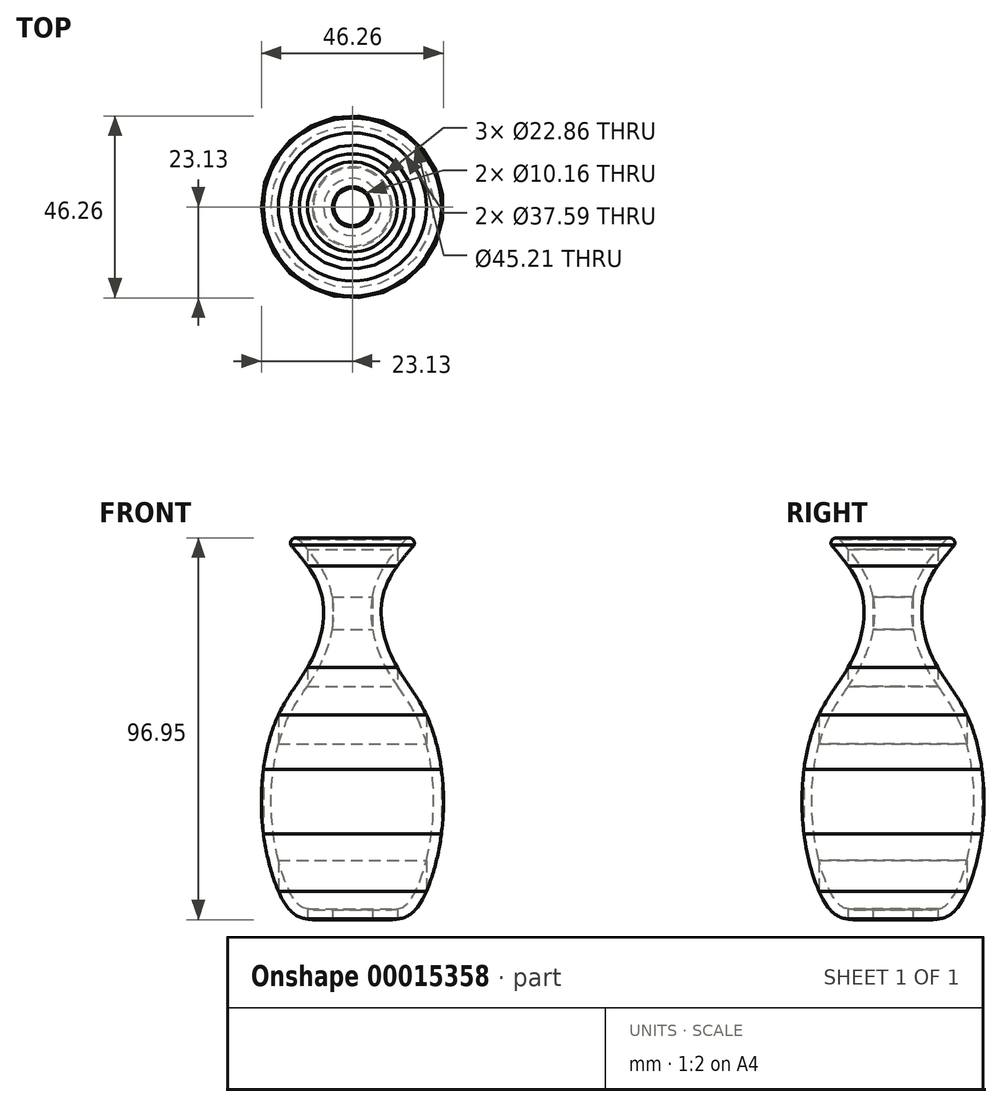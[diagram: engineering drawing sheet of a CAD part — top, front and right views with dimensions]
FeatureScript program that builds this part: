
annotation { "Feature Type Name" : "Feature", "Feature Type Description" : "" }
export const myFeature = defineFeature(function(context is Context, id is Id, definition is map)
    precondition{}
    {
        {
            var Q0;
            Q0=qCreatedBy(makeId("Top.planeOp"),FACE);
            var sketch = newSketch(context, id + "F0", { "sketchPlane" : qUnion([Q0])});
            skCircle(sketch, "E0", {"center": v(0, 0) * mm, "radius": 28.58 * mm});
            skCircle(sketch, "E1", {"center": v(0, 0) * mm, "radius": 12.7 * mm});
            skCircle(sketch, "E2", {"center": v(0, 0) * mm, "radius": 47 * mm});
            skCircle(sketch, "E3", {"center": v(0, 0) * mm, "radius": 56.52 * mm});
            skCircle(sketch, "E4", {"center": v(0, 0) * mm, "radius": 63.5 * mm});
            skSolve(sketch);
        }
        {
            var Q0;
            Q0 = qSketchRegion(id + "F0", true);
            extrude(context, id + "F1", {"entities" : qUnion([Q0]), "depth" : 254 * mm});
        }
        {
            var Q0;
            Q0=makeQuery(id+"F0.imprint","IMPRINT",FACE,{"disambiguationData":[TD([[makeQuery(id+"F0.imprint","IMPRINT",EDGE,{"derivedFrom":sQuery(id+"F0.wireOp",EDGE,"E2")}),-1.0]])]});
            var Q1;
            Q1=makeQuery(id+"F0.imprint","IMPRINT",FACE,{"disambiguationData":[TD([[makeQuery(id+"F0.imprint","IMPRINT",EDGE,{"derivedFrom":sQuery(id+"F0.wireOp",EDGE,"E0")}),1.0]])]});
            extrude(context, id + "F2", {"entities" : qUnion([Q0, Q1]), "depth" : 254 * mm});
        }
        {
            var Q0;
            Q0=makeQuery(id+"F0.imprint","IMPRINT",FACE,{"disambiguationData":[TD([[makeQuery(id+"F0.imprint","IMPRINT",EDGE,{"derivedFrom":sQuery(id+"F0.wireOp",EDGE,"E0")}),-1.0]])]});
            var Q1;
            Q1=makeQuery(id+"F0.imprint","IMPRINT",FACE,{"disambiguationData":[TD([[makeQuery(id+"F0.imprint","IMPRINT",EDGE,{"derivedFrom":sQuery(id+"F0.wireOp",EDGE,"E1")}),1.0]])]});
            extrude(context, id + "F3", {"entities" : qUnion([Q0, Q1]), "depth" : 254 * mm});
        }
        {
            var Q0;
            Q0=qCreatedBy(makeId("Front.planeOp"),FACE);
            var sketch = newSketch(context, id + "F4", { "sketchPlane" : qUnion([Q0])});
            skLineSegment(sketch, "E5", {"start": v(25.4, 0) * mm, "end": v(-23.74, 0) * mm});
            skFitSpline(sketch, "E6", {"points": [v(25.4, 0) * mm, v(38.83, 5.12) * mm, v(57.14, 60.04) * mm, v(47.11, 129.79) * mm, v(25.4, 165.97) * mm, v(19.65, 206.94) * mm, v(41.88, 241.3) * mm], "startDerivative": vector(142.07, 14.8) * mm, "endDerivative": vector(170.63, 209.79) * mm});
            skLineSegment(sketch, "E7", {"start": v(0, 241.3) * mm, "end": v(0, 0) * mm});
            skFitSpline(sketch, "E8.0", {"points": [v(24.74, 6.32) * mm, v(25.48, 6.4) * mm, v(26.87, 6.55) * mm, v(28.68, 6.82) * mm, v(30.23, 7.18) * mm, v(31.57, 7.67) * mm, v(32.6, 8.24) * mm, v(33.46, 8.84) * mm, v(34, 9.3) * mm, v(34.46, 9.74) * mm, v(34.93, 10.22) * mm, v(35.56, 10.93) * mm, v(36.36, 11.95) * mm, v(37.45, 13.51) * mm, v(38.85, 15.83) * mm, v(40.53, 19.14) * mm, v(42.16, 22.9) * mm, v(44.25, 28.42) * mm, v(46.61, 36.18) * mm, v(48.91, 46.4) * mm, v(50.29, 55.33) * mm, v(51, 62.52) * mm, v(51.46, 69.72) * mm, v(51.55, 78.66) * mm, v(50.93, 89.17) * mm, v(49.63, 99.3) * mm, v(47.68, 108.9) * mm, v(45.56, 116.33) * mm, v(43.6, 121.84) * mm, v(42, 125.74) * mm, v(40.3, 129.37) * mm, v(38.45, 132.84) * mm, v(36.5, 136.18) * mm, v(33.77, 140.5) * mm, v(30.19, 145.8) * mm, v(26.53, 151.22) * mm, v(23.68, 155.79) * mm, v(21.96, 158.77) * mm, v(20.64, 161.25) * mm, v(19.69, 163.16) * mm, v(18.77, 165.12) * mm, v(17.62, 167.78) * mm, v(16.3, 171.2) * mm, v(14.47, 176.84) * mm, v(12.75, 184.1) * mm, v(11.93, 191.53) * mm, v(11.9, 197.46) * mm, v(12.21, 201.88) * mm, v(12.78, 205.52) * mm, v(13.44, 208.4) * mm, v(14.23, 211.22) * mm, v(15.45, 214.6) * mm, v(17.82, 219.78) * mm, v(21.42, 225.79) * mm, v(26.38, 232.5) * mm, v(31.66, 238.93) * mm, v(35.2, 243.17) * mm, v(36.95, 245.31) * mm]});
            skLineSegment(sketch, "E9", {"start": v(24.74, 6.32) * mm, "end": v(0, 6.32) * mm});
            skLineSegment(sketch, "E10", {"start": v(0, 241.3) * mm, "end": v(33.56, 241.2) * mm});
            skArc(sketch, "E11", {"start": v(33.56, 241.2) * mm, "mid": v(37.7, 241.95) * mm, "end": v(39.15, 237.98) * mm});
            skSolve(sketch);
        }
        {
            var Q0;
            {var subQ8=sQuery(id+"F4.wireOp",EDGE,"E6");Q0=makeQuery(id+"F4.imprint","IMPRINT",FACE,{"disambiguationData":[TD([[makeQuery(id+"F4.imprint","IMPRINT",EDGE,{"derivedFrom":subQ8}),1.0]])]});}
            var Q1;
            Q1=sQuery(id+"F4.wireOp",EDGE,"E7");
            revolve(context, id + "F5", {"operationType" : NewBodyOperationType.INTERSECT, "entities" : qUnion([Q0]), "axis" : qUnion([Q1]), "revolveType" : RevolveType.FULL, "oppositeDirection" : true});
        }
        {
            var Q0;
            Q0=makeQuery(id+"F1.opExtrude","SWEPT_BODY",BODY,{"disambiguationData":[OSD([sQuery(id+"F0.wireOp",EDGE,"E3"),sQuery(id+"F0.wireOp",EDGE,"E4")])]});
            var Q1;
            Q1=makeQuery(id+"F2.opExtrude","SWEPT_BODY",BODY,{"disambiguationData":[OSD([sQuery(id+"F0.wireOp",EDGE,"E2"),sQuery(id+"F0.wireOp",EDGE,"E3")])]});
            var Q2;
            Q2=makeQuery(id+"F5.boolean.opBoolean","SPLIT",BODY,{"disambiguationData":[OD(0.0)],"derivedFrom":makeQuery(id+"F2.opExtrude","SWEPT_BODY",BODY,{"disambiguationData":[OSD([sQuery(id+"F0.wireOp",EDGE,"E0"),sQuery(id+"F0.wireOp",EDGE,"E1")])]})});
            var Q3;
            Q3=makeQuery(id+"F5.boolean.opBoolean","SPLIT",BODY,{"disambiguationData":[OD(1.0)],"derivedFrom":makeQuery(id+"F2.opExtrude","SWEPT_BODY",BODY,{"disambiguationData":[OSD([sQuery(id+"F0.wireOp",EDGE,"E0"),sQuery(id+"F0.wireOp",EDGE,"E1")])]})});
            var Q4;
            Q4=makeQuery(id+"F5.boolean.opBoolean","SPLIT",BODY,{"disambiguationData":[OD(0.0)],"derivedFrom":makeQuery(id+"F3.opExtrude","SWEPT_BODY",BODY,{"disambiguationData":[OSD([sQuery(id+"F0.wireOp",EDGE,"E0"),sQuery(id+"F0.wireOp",EDGE,"E2")])]})});
            var Q5;
            Q5=makeQuery(id+"F5.boolean.opBoolean","SPLIT",BODY,{"disambiguationData":[OD(0.0)],"derivedFrom":makeQuery(id+"F3.opExtrude","SWEPT_BODY",BODY,{"disambiguationData":[OSD([sQuery(id+"F0.wireOp",EDGE,"E1")])]})});
            var Q6;
            Q6=makeQuery(id+"F5.boolean.opBoolean","SPLIT",BODY,{"disambiguationData":[OD(1.0)],"derivedFrom":makeQuery(id+"F3.opExtrude","SWEPT_BODY",BODY,{"disambiguationData":[OSD([sQuery(id+"F0.wireOp",EDGE,"E1")])]})});
            var Q7;
            Q7=makeQuery(id+"F5.boolean.opBoolean","SPLIT",BODY,{"disambiguationData":[OD(1.0)],"derivedFrom":makeQuery(id+"F3.opExtrude","SWEPT_BODY",BODY,{"disambiguationData":[OSD([sQuery(id+"F0.wireOp",EDGE,"E0"),sQuery(id+"F0.wireOp",EDGE,"E2")])]})});
            var Q8;
            Q8=makeQuery(id+"F5.boolean.opBoolean","SPLIT",BODY,{"disambiguationData":[OD(2.0)],"derivedFrom":makeQuery(id+"F3.opExtrude","SWEPT_BODY",BODY,{"disambiguationData":[OSD([sQuery(id+"F0.wireOp",EDGE,"E0"),sQuery(id+"F0.wireOp",EDGE,"E2")])]})});
            var Q9;
            Q9=qCreatedBy(makeId("Origin.pointOp"),VERTEX);
            transform(context, id + "F6", {"entities" : qUnion([Q0, Q1, Q2, Q3, Q4, Q5, Q6, Q7, Q8]), "transformType" : TransformType.SCALE_UNIFORMLY, "scale" : 0.4, "makeCopy" : false, "scalePoint" : qUnion([Q9])});
        }
    });
